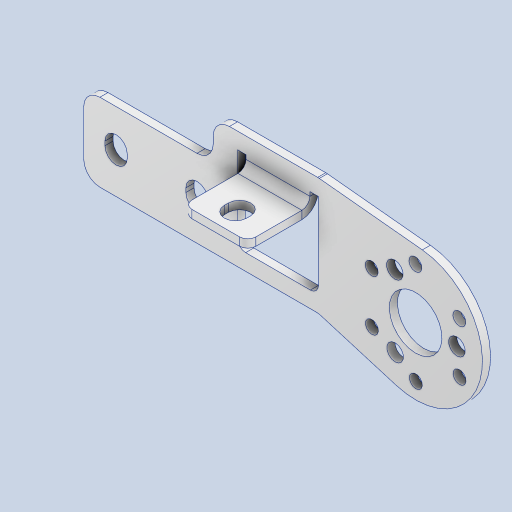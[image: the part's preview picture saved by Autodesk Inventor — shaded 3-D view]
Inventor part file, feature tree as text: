
AUTODESK INVENTOR PART (.ipt)
format: ipt  version: 2023 (Build 270158000, 158)  size: 1,525,248 bytes
history: native  units: mm
features: other x5, extrude x2, fillet x2, sketch x2
ambient origin geometry x8: Origin, YZ Plane, XZ Plane, XY Plane, X Axis, Y Axis, Z Axis, Center Point
bodies: Body1 (feature_tree), Body2 (feature_tree)
feature tree (11):
  other  "GIM8108-8_1.ipt"
  extrude  "押し出し8"  Depth=10.0mm
  other  "折り曲げ8"
  fillet  "フィレット6"  Radius=4.1mm
  extrude  "押し出し9"  Depth=3.2mm
  fillet  "フィレット7"  Radius=60.0mm
  other  "TaggingFeature1"
  sketch  "スケッチ22"
  sketch  "スケッチ23"
  other  "ソリッド1::GIM8108-8_1.ipt"
  other  "Srf1"
